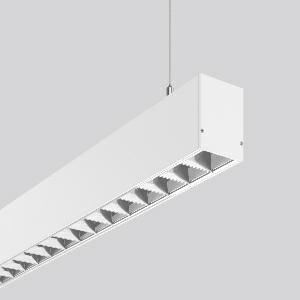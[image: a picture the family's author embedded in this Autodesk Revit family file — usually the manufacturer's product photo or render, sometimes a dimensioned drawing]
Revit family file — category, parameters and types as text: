
# Revit family: less_is_more_50_312338_002_76_a7a1
name_source: partatom
category: Lighting Fixtures
units: mm (PartAtom-declared; Revit-internal decimal feet)

## family parameters
Cut with Voids When Loaded = No
Host = Face
Light Source = No
Part Type = Normal
Room Calculation Point = No
Round Connector Dimension = Use Diameter
Shared = No

## types (1)
- LESS IS MORE 50 (1 x LED Modul 830, 5050 lm, 3000)
    Apparent Load = 41 VA
    CIE Flux Codes = 95 100 100 100 100
    Color Rendering = 80
    Color Temperature = 3000
    Default Elevation = 1800 mm
    Description = Series: LESS IS MORE 50
Linear pendant luminaire for aesthetically sophisticated lighting. Housing: extruded aluminium profile, powder-coated. End cap aluminium powder-coated. Canopy made of aluminium, powder-coated. Alea optical system: Reflector structure (ABS, Aluminium-coated, highly polished) with integrated diffuser made of non-yellowing plastic (PMMA) opal for glare-free light at the workstation (screen-compliant according to EN 12464-1). Direct light emission. Suitable for pendant. 2-point steel cable suspension freely positionable and infinitely height-adjustable. Special lengths available on request. LED unit with integrated converter interchangeable and removable. Suitable for through-wiring. With sensors or as a safety luminaire on request. 
Colour: traffic white, matt (RAL 9016)
Length: 1687 mm
Width: 57 mm
Height: 75 mm
Suspension length: 2000 mm
Lamp: LED
Socket: without socket
Colour temperature: 3000K
Colour rendering index (CRI): 80
System power: 41 W
Rated luminous flux: 5050 lm
Luminous efficiency: 123 lm/W
Control gear: Converter, dimmable, DALI
Protection class: I
Type of protection: IP 20
    Height = 75 mm
    Lamp = 1 x LED Modul 830
    Lamp Light Flux = 5050 lm
    Lamp count = 1
    Length = 1687 mm
    Lifetime = 50000 h
    Luminous efficacy = 123 lm/W
    Manufacturer = RZB
    ModVariant = No
    Model = 312338.002.76
    Mounting Place = Ceiling
    Mounting Type = Pendant
    Number of Poles = 1
    OnlyDefault = Yes
    Power Factor = 1
    Product Name = LESS IS MORE 50
    Product group = Pendant LED linear luminaires
    ProductGroupID = 907
    Protection Class = Protection class I
    Protection Degree = IP 20
    RLX_Detail_Level = 1
    RLX_Emergency_Light_Flux = 0 lm
    RLX_Emergency_Type = 0
    RLX_Emergency_Type_DB = No
    RlxData = <blob elided: 33137 chars, md5=b57b32a8>
    Socket = socket
    Standby Power = 0 W
    System Light Flux = 5050 lm
    System Power = 41 W
    Type Comments = Product without accessories
    Type Image = 312342.002.jpg
    URL = http://relux.com
    VarID = ---
    Voltage = 230 V
    Voltage Range = 220-240 V
    Weight = 0.00 kg
    Width = 57 mm

## geometry (parser evidence)
native form markers: Blend x4, Sweep x8
no freeform markers — native parametric forms only
